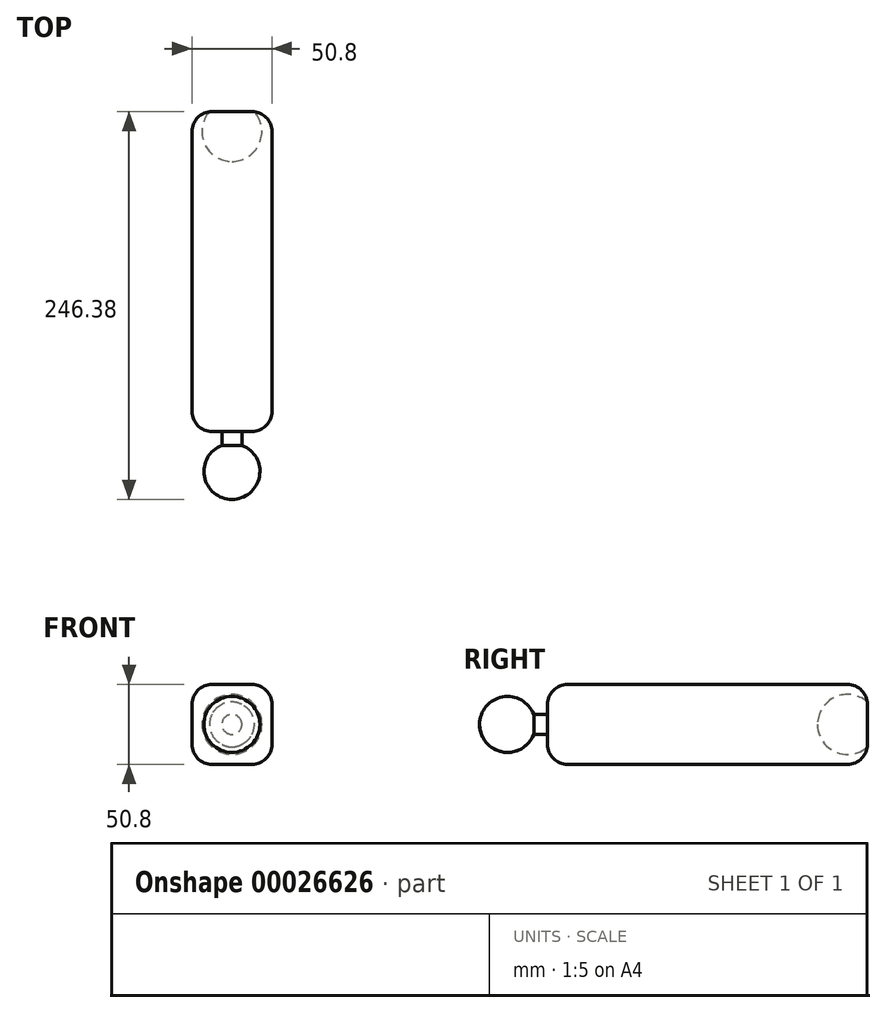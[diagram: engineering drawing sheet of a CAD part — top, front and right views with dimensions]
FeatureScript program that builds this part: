
annotation { "Feature Type Name" : "Feature", "Feature Type Description" : "" }
export const myFeature = defineFeature(function(context is Context, id is Id, definition is map)
    precondition{}
    {
        {
            var Q0;
            Q0=qCreatedBy(makeId("Front.planeOp"),FACE);
            var sketch = newSketch(context, id + "F0", { "sketchPlane" : qUnion([Q0])});
            skLineSegment(sketch, "E0.bottom", {"start": v(0, 0) * mm, "end": v(50.8, 0) * mm});
            skLineSegment(sketch, "E0.top", {"start": v(0, 50.8) * mm, "end": v(50.8, 50.8) * mm});
            skLineSegment(sketch, "E0.left", {"start": v(0, 0) * mm, "end": v(0, 50.8) * mm});
            skLineSegment(sketch, "E0.right", {"start": v(50.8, 0) * mm, "end": v(50.8, 50.8) * mm});
            skSolve(sketch);
        }
        {
            var Q0;
            Q0 = qSketchRegion(id + "F0", true);
            extrude(context, id + "F1", {"entities" : qUnion([Q0]), "depth" : 203.2 * mm});
        }
        {
            var Q0;
            Q0=makeQuery(id+"F1.opExtrude","SWEPT_FACE",FACE,{"disambiguationData":[OSD([sQuery(id+"F0.wireOp",EDGE,"E0.bottom")])]});
            var Q1;
            Q1=makeQuery(id+"F1.opExtrude","SWEPT_FACE",FACE,{"disambiguationData":[OSD([sQuery(id+"F0.wireOp",EDGE,"E0.left")])]});
            var Q2;
            Q2=makeQuery(id+"F1.opExtrude","SWEPT_FACE",FACE,{"disambiguationData":[OSD([sQuery(id+"F0.wireOp",EDGE,"E0.top")])]});
            var Q3;
            Q3=makeQuery(id+"F1.opExtrude","SWEPT_FACE",FACE,{"disambiguationData":[OSD([sQuery(id+"F0.wireOp",EDGE,"E0.right")])]});
            fillet(context, id + "F2", {"entities" : qUnion([Q0, Q1, Q2, Q3]), "radius" : 12.7 * mm, "tangentPropagation" : true, "allowEdgeOverflow" : false});
        }
        {
            var Q0;
            Q0=makeQuery(id+"F1.opExtrude","SWEPT_FACE",FACE,{"disambiguationData":[OSD([sQuery(id+"F0.wireOp",EDGE,"E0.right")])]});
            var Q1;
            Q1=makeQuery(id+"F1.opExtrude","SWEPT_FACE",FACE,{"disambiguationData":[OSD([sQuery(id+"F0.wireOp",EDGE,"E0.left")])]});
            cPlane(context, id + "F3", {"entities" : qUnion([Q0, Q1]), "cplaneType" : CPlaneType.MID_PLANE, "offset" : 152.4 * mm, "width" : 152.4 * mm, "height" : 152.4 * mm});
        }
        {
            var Q0;
            Q0=makeQuery(id+"F1.opExtrude","CAP_FACE",FACE,{"disambiguationData":[OSD([sQuery(id+"F0.wireOp",EDGE,"E0.bottom"),sQuery(id+"F0.wireOp",EDGE,"E0.top"),sQuery(id+"F0.wireOp",EDGE,"E0.left"),sQuery(id+"F0.wireOp",EDGE,"E0.right")])],"isStart":false});
            var sketch = newSketch(context, id + "F4", { "sketchPlane" : qUnion([Q0])});
            skCircle(sketch, "E1", {"center": v(25.4, 25.4) * mm, "radius": 6.35 * mm});
            skSolve(sketch);
        }
        {
            var Q0;
            Q0 = qSketchRegion(id + "F4", true);
            extrude(context, id + "F5", {"entities" : qUnion([Q0]), "operationType" : NewBodyOperationType.ADD, "depth" : 12.7 * mm});
        }
        {
            var Q0;
            Q0=qCreatedBy(id+"F3.planeOp",FACE);
            var sketch = newSketch(context, id + "F6", { "sketchPlane" : qUnion([Q0])});
            skPoint(sketch, "E2", {"position": v(-228.6, 25.4) * mm});
            skArc(sketch, "E3", {"start": v(-246.38, 25.4) * mm, "mid": v(-228.6, 7.62) * mm, "end": v(-210.82, 25.4) * mm});
            skLineSegment(sketch, "E4", {"start": v(-228.6, 25.4) * mm, "end": v(-210.82, 25.4) * mm});
            skLineSegment(sketch, "E5", {"start": v(-228.6, 25.4) * mm, "end": v(-246.38, 25.4) * mm});
            skSolve(sketch);
        }
        {
            var Q0;
            Q0=makeQuery(id+"F6.imprint","IMPRINT",FACE,{"disambiguationData":[TD([[makeQuery(id+"F6.imprint","IMPRINT",EDGE,{"derivedFrom":sQuery(id+"F6.wireOp",EDGE,"E3")}),1.0]])]});
            var Q1;
            Q1=sQuery(id+"F6.wireOp",EDGE,"E5");
            revolve(context, id + "F7", {"operationType" : NewBodyOperationType.ADD, "entities" : qUnion([Q0]), "axis" : qUnion([Q1]), "revolveType" : RevolveType.FULL});
        }
        {
            var Q0;
            Q0=qCreatedBy(id+"F3.planeOp",FACE);
            var sketch = newSketch(context, id + "F8", { "sketchPlane" : qUnion([Q0])});
            skArc(sketch, "E6", {"start": v(-31.75, 25.4) * mm, "mid": v(-12.7, 6.35) * mm, "end": v(6.35, 25.4) * mm});
            skLineSegment(sketch, "E7", {"start": v(-12.7, 25.4) * mm, "end": v(6.35, 25.4) * mm});
            skLineSegment(sketch, "E8", {"start": v(6.35, 25.4) * mm, "end": v(-31.75, 25.4) * mm});
            skSolve(sketch);
        }
        {
            var Q0;
            Q0 = qSketchRegion(id + "F8", true);
            var Q1;
            Q1=sQuery(id+"F8.wireOp",EDGE,"E7");
            revolve(context, id + "F9", {"operationType" : NewBodyOperationType.REMOVE, "entities" : qUnion([Q0]), "axis" : qUnion([Q1]), "revolveType" : RevolveType.FULL, "oppositeDirection" : true});
        }
    });
